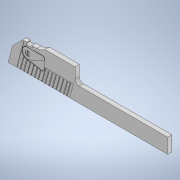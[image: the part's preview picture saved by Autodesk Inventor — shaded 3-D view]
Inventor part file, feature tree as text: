
AUTODESK INVENTOR PART (.ipt)
format: ipt  version: 2022 (Build 260153000, 153)  size: 397,312 bytes
history: native  units: in
note: dims shown in document units (in); Inventor stores cm internally (conversion verified against a paired STEP export)
features: extrude x4, sketch x2, sheet_metal_op x1, plane x1, mirror x1, other x1
ambient origin geometry x8: Origin, YZ Plane, XZ Plane, XY Plane, X Axis, Y Axis, Z Axis, Center Point
bodies: Solid1 (feature_tree)
feature tree (10):
  sheet_metal_op  "Face1"
  sketch  "Sketch2"  dims[d7=0.0039in d8=0.0in d9=0.0039in d10=0.0in d11=0.0039in d12=0.0in]
  extrude  "Extrusion1"  Depth=0.0039in TaperAngle=0.0deg
  extrude  "Extrusion4"  Depth=0.0039in TaperAngle=0.0deg
  extrude  "Extrusion5"  Depth=0.0039in TaperAngle=0.0deg
  extrude  "Extrusion6"  [1 undecoded]
  plane  "Work Plane1"
  mirror  "Mirror1"
  sketch  "Sketch1"  dims[d0=0.0591in d1=0.0039in d2=0.0in]
  other  "Plate1"
note: 1 required parameter value undecoded (feature->parameter linkage not recoverable at this tier; creation-order binding heuristic only, values carry confidence <= 0.55)
